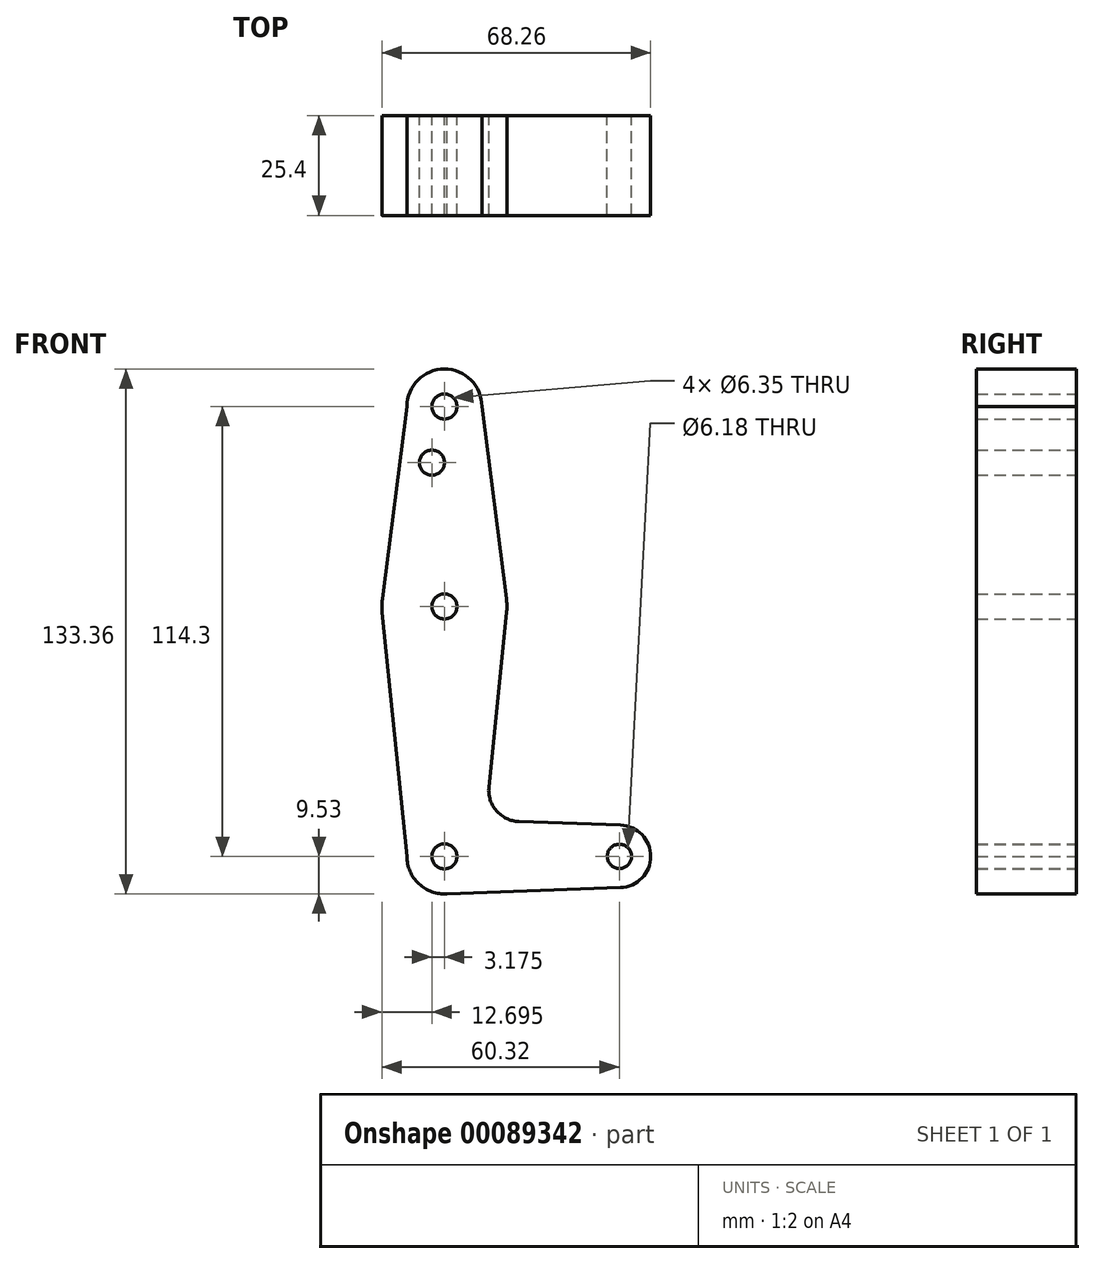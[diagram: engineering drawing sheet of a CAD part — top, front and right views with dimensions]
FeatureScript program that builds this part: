
annotation { "Feature Type Name" : "Feature", "Feature Type Description" : "" }
export const myFeature = defineFeature(function(context is Context, id is Id, definition is map)
    precondition{}
    {
        {
            var Q0;
            Q0=qCreatedBy(makeId("Front.planeOp"),FACE);
            var sketch = newSketch(context, id + "F0", { "sketchPlane" : qUnion([Q0])});
            skCircle(sketch, "E0", {"center": v(0, 114.3) * mm, "radius": 9.53 * mm});
            skCircle(sketch, "E1", {"center": v(0, 63.5) * mm, "radius": 15.88 * mm});
            skCircle(sketch, "E2", {"center": v(0, 0) * mm, "radius": 9.53 * mm});
            skCircle(sketch, "E3", {"center": v(44.45, 0) * mm, "radius": 7.94 * mm});
            skLineSegment(sketch, "E4", {"start": v(0, 114.3) * mm, "end": v(0, 0) * mm});
            skLineSegment(sketch, "E5", {"start": v(44.45, 0) * mm, "end": v(0, 0) * mm});
            skLineSegment(sketch, "E6", {"start": v(9.53, 114.3) * mm, "end": v(15.75, 65.5) * mm});
            skLineSegment(sketch, "E7", {"start": v(-9.53, 114.3) * mm, "end": v(-15.75, 65.5) * mm});
            skLineSegment(sketch, "E8", {"start": v(11.3, 17.6) * mm, "end": v(15.8, 61.9) * mm});
            skLineSegment(sketch, "E9", {"start": v(-9.52, 0) * mm, "end": v(-15.8, 61.9) * mm});
            skLineSegment(sketch, "E10", {"start": v(0, -9.53) * mm, "end": v(44.73, -7.93) * mm});
            skLineSegment(sketch, "E11", {"start": v(18.93, 8.85) * mm, "end": v(44.73, 7.93) * mm});
            skCircle(sketch, "E12", {"center": v(0, 114.3) * mm, "radius": 3.18 * mm});
            skCircle(sketch, "E13", {"center": v(-3.17, 100.03) * mm, "radius": 3.18 * mm});
            skCircle(sketch, "E14", {"center": v(0, 63.5) * mm, "radius": 3.18 * mm});
            skCircle(sketch, "E15", {"center": v(0, 0) * mm, "radius": 3.18 * mm});
            skCircle(sketch, "E16", {"center": v(44.45, 0) * mm, "radius": 3.09 * mm});
            skPoint(sketch, "E17.newPointB", {"position": v(0, 9.53) * mm});
            skArc(sketch, "E17.filletArc", {"start": v(11.3, 17.6) * mm, "mid": v(13.22, 11.57) * mm, "end": v(18.93, 8.85) * mm});
            skSolve(sketch);
        }
        {
            var Q0;
            Q0 = qSketchRegion(id + "F0", true);
            var Q1;
            {var subQ0=sQuery(id+"F0.wireOp",EDGE,"E4");var subQ1=sQuery(id+"F0.wireOp",EDGE,"E2");var subQ2=makeQuery(id+"F0.imprint","INTERSECT",VERTEX,{"derivedFrom":[subQ1,subQ0]});Q1=makeQuery(id+"F0.imprint","IMPRINT",FACE,{"disambiguationData":[TD([[makeQuery(id+"F0.imprint","IMPRINT",EDGE,{"disambiguationData":[TD([[subQ2,1.0]])],"derivedFrom":subQ1}),1.0]])]});}
            extrude(context, id + "F1", {"entities" : qUnion([Q0, Q1]), "depth" : 25.4 * mm});
        }
    });
